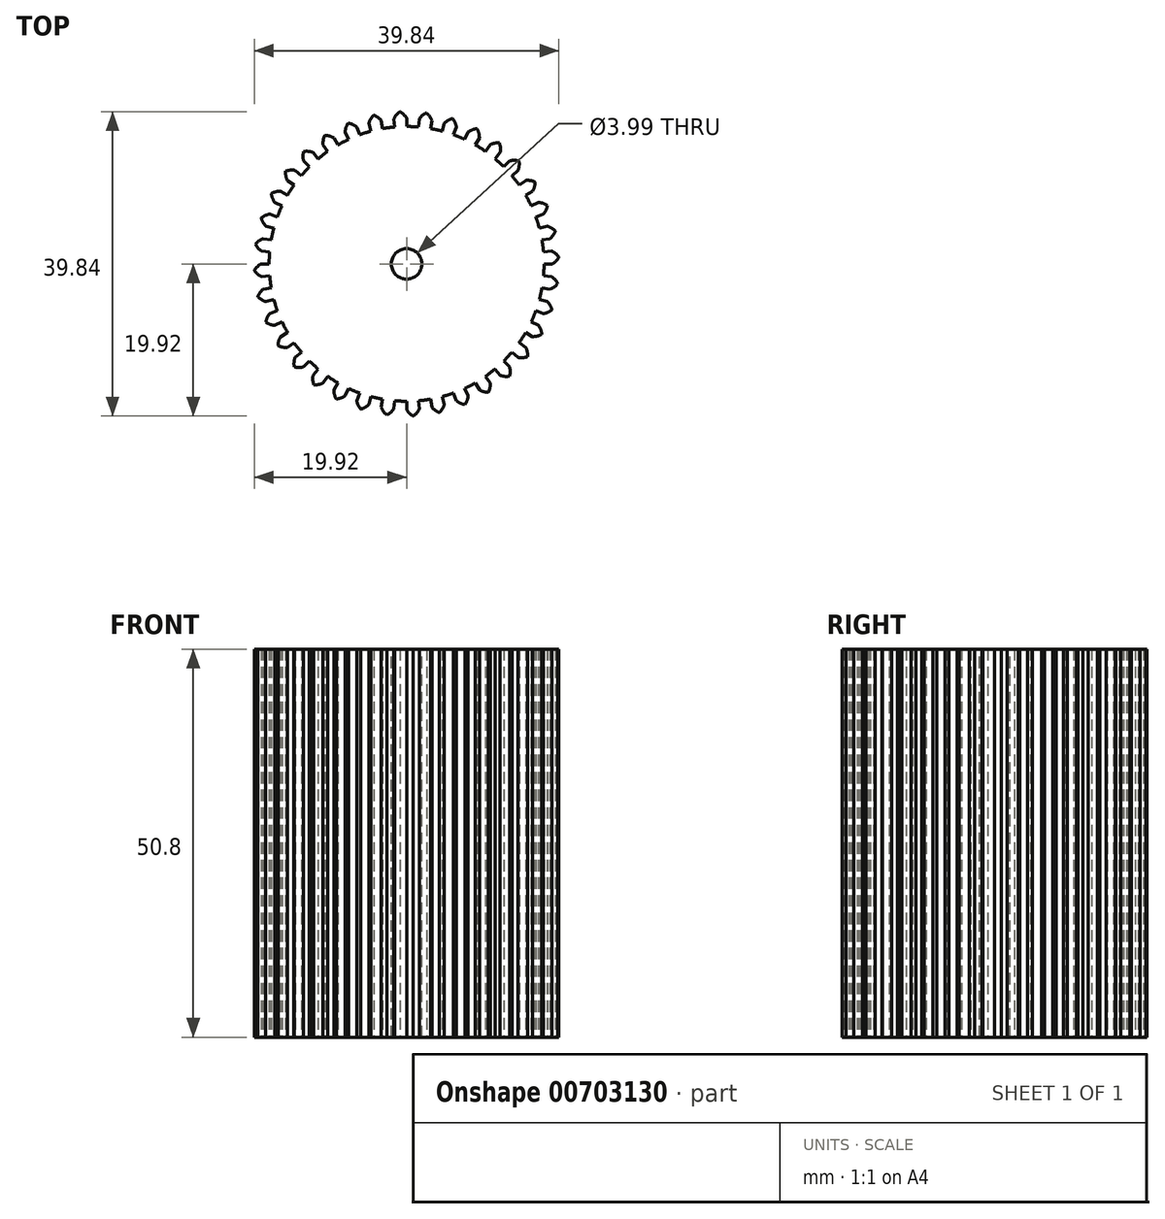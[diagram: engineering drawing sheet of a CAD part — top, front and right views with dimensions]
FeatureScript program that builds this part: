
annotation { "Feature Type Name" : "Feature", "Feature Type Description" : "" }
export const myFeature = defineFeature(function(context is Context, id is Id, definition is map)
    precondition{}
    {
        {
            var Q0;
            Q0=qCreatedBy(makeId("Top.planeOp"),FACE);
            var sketch = newSketch(context, id + "F0", { "sketchPlane" : qUnion([Q0])});
            skArc(sketch, "E0", {"start": v(-1.57, 17.91) * mm, "mid": v(0.78, -17.97) * mm, "end": v(0, 17.98) * mm});
            skPoint(sketch, "E1", {"position": v(0, 19.05) * mm});
            skArc(sketch, "E2.trimOffspring", {"start": v(0, 19.05) * mm, "mid": v(-0.38, 19.54) * mm, "end": v(-0.87, 19.92) * mm});
            skArc(sketch, "E3.trimOffspring", {"start": v(0, 16.67) * mm, "mid": v(0, 16.67) * mm, "end": v(0, 16.67) * mm});
            skArc(sketch, "E4.trimOffspring", {"start": v(-4.4, 17.45) * mm, "mid": v(-4.4, 17.44) * mm, "end": v(-4.4, 17.43) * mm});
            skArc(sketch, "E5.trimOffspring", {"start": v(0, 16.67) * mm, "mid": v(0, 16.67) * mm, "end": v(0, 16.68) * mm});
            skLineSegment(sketch, "E6", {"start": v(0, 19.05) * mm, "end": v(0, 17.98) * mm});
            skArc(sketch, "E7.MirrorCS", {"start": v(-1.66, 18.98) * mm, "mid": v(-1.33, 19.5) * mm, "end": v(-0.87, 19.92) * mm});
            skLineSegment(sketch, "E8", {"start": v(-1.66, 18.98) * mm, "end": v(-1.57, 17.91) * mm});
            skLineSegment(sketch, "E9.1.0", {"start": v(-3.3, 18.76) * mm, "end": v(-3.12, 17.7) * mm});
            skArc(sketch, "E9.1.1", {"start": v(-3.3, 18.76) * mm, "mid": v(-3.77, 19.18) * mm, "end": v(-4.32, 19.47) * mm});
            skArc(sketch, "E9.1.2", {"start": v(-4.93, 18.4) * mm, "mid": v(-4.7, 18.98) * mm, "end": v(-4.32, 19.47) * mm});
            skLineSegment(sketch, "E9.1.3", {"start": v(-4.93, 18.4) * mm, "end": v(-4.65, 17.37) * mm});
            skLineSegment(sketch, "E9.2.0", {"start": v(-6.52, 17.9) * mm, "end": v(-6.15, 16.9) * mm});
            skArc(sketch, "E9.2.1", {"start": v(-6.52, 17.9) * mm, "mid": v(-7.04, 18.24) * mm, "end": v(-7.63, 18.42) * mm});
            skArc(sketch, "E9.2.2", {"start": v(-8.05, 17.27) * mm, "mid": v(-7.92, 17.87) * mm, "end": v(-7.63, 18.42) * mm});
            skLineSegment(sketch, "E9.2.3", {"start": v(-8.05, 17.27) * mm, "end": v(-7.6, 16.3) * mm});
            skLineSegment(sketch, "E10.2.3.0", {"start": v(-9.52, 16.5) * mm, "end": v(-9, 15.57) * mm});
            skArc(sketch, "E10.3.3.0", {"start": v(-9.52, 16.5) * mm, "mid": v(-10.1, 16.74) * mm, "end": v(-10.72, 16.82) * mm});
            skArc(sketch, "E10.7.3.0", {"start": v(-10.93, 15.6) * mm, "mid": v(-10.9, 16.23) * mm, "end": v(-10.72, 16.82) * mm});
            skLineSegment(sketch, "E10.11.3.0", {"start": v(-10.93, 15.6) * mm, "end": v(-10.31, 14.73) * mm});
            skLineSegment(sketch, "E10.2.4.0", {"start": v(-12.25, 14.6) * mm, "end": v(-11.56, 13.78) * mm});
            skArc(sketch, "E10.3.4.0", {"start": v(-12.25, 14.6) * mm, "mid": v(-12.85, 14.73) * mm, "end": v(-13.47, 14.7) * mm});
            skArc(sketch, "E10.7.4.0", {"start": v(-13.47, 13.47) * mm, "mid": v(-13.55, 14.09) * mm, "end": v(-13.47, 14.7) * mm});
            skLineSegment(sketch, "E10.11.4.0", {"start": v(-13.47, 13.47) * mm, "end": v(-12.72, 12.72) * mm});
            skLineSegment(sketch, "E10.2.5.0", {"start": v(-14.6, 12.25) * mm, "end": v(-13.78, 11.56) * mm});
            skArc(sketch, "E10.3.5.0", {"start": v(-14.6, 12.25) * mm, "mid": v(-15.21, 12.27) * mm, "end": v(-15.82, 12.14) * mm});
            skArc(sketch, "E10.7.5.0", {"start": v(-15.6, 10.93) * mm, "mid": v(-15.8, 11.52) * mm, "end": v(-15.82, 12.14) * mm});
            skLineSegment(sketch, "E10.11.5.0", {"start": v(-15.6, 10.93) * mm, "end": v(-14.73, 10.31) * mm});
            skLineSegment(sketch, "E10.2.6.0", {"start": v(-16.5, 9.53) * mm, "end": v(-15.57, 9) * mm});
            skArc(sketch, "E10.3.6.0", {"start": v(-16.5, 9.53) * mm, "mid": v(-17.11, 9.45) * mm, "end": v(-17.69, 9.2) * mm});
            skArc(sketch, "E10.7.6.0", {"start": v(-17.27, 8.05) * mm, "mid": v(-17.55, 8.6) * mm, "end": v(-17.69, 9.2) * mm});
            skLineSegment(sketch, "E10.11.6.0", {"start": v(-17.27, 8.05) * mm, "end": v(-16.3, 7.6) * mm});
            skLineSegment(sketch, "E10.2.7.0", {"start": v(-17.9, 6.52) * mm, "end": v(-16.9, 6.15) * mm});
            skArc(sketch, "E10.3.7.0", {"start": v(-17.9, 6.52) * mm, "mid": v(-18.5, 6.33) * mm, "end": v(-19.02, 6) * mm});
            skArc(sketch, "E10.7.7.0", {"start": v(-18.4, 4.93) * mm, "mid": v(-18.78, 5.42) * mm, "end": v(-19.02, 6) * mm});
            skLineSegment(sketch, "E10.11.7.0", {"start": v(-18.4, 4.93) * mm, "end": v(-17.37, 4.65) * mm});
            skLineSegment(sketch, "E10.2.8.0", {"start": v(-18.76, 3.3) * mm, "end": v(-17.7, 3.12) * mm});
            skArc(sketch, "E10.3.8.0", {"start": v(-18.76, 3.3) * mm, "mid": v(-19.31, 3.02) * mm, "end": v(-19.77, 2.6) * mm});
            skArc(sketch, "E10.7.8.0", {"start": v(-18.98, 1.66) * mm, "mid": v(-19.44, 2.08) * mm, "end": v(-19.77, 2.6) * mm});
            skLineSegment(sketch, "E10.11.8.0", {"start": v(-18.98, 1.66) * mm, "end": v(-17.91, 1.57) * mm});
            skLineSegment(sketch, "E10.2.9.0", {"start": v(-19.05, 0) * mm, "end": v(-17.98, 0) * mm});
            skArc(sketch, "E10.3.9.0", {"start": v(-19.05, 0) * mm, "mid": v(-19.54, -0.38) * mm, "end": v(-19.92, -0.87) * mm});
            skArc(sketch, "E10.7.9.0", {"start": v(-18.98, -1.66) * mm, "mid": v(-19.5, -1.33) * mm, "end": v(-19.92, -0.87) * mm});
            skLineSegment(sketch, "E10.11.9.0", {"start": v(-18.98, -1.66) * mm, "end": v(-17.91, -1.57) * mm});
            skLineSegment(sketch, "E10.2.10.0", {"start": v(-18.76, -3.3) * mm, "end": v(-17.7, -3.12) * mm});
            skArc(sketch, "E10.3.10.0", {"start": v(-18.76, -3.3) * mm, "mid": v(-19.18, -3.77) * mm, "end": v(-19.47, -4.32) * mm});
            skArc(sketch, "E10.7.10.0", {"start": v(-18.4, -4.93) * mm, "mid": v(-18.98, -4.7) * mm, "end": v(-19.47, -4.32) * mm});
            skLineSegment(sketch, "E10.11.10.0", {"start": v(-18.4, -4.93) * mm, "end": v(-17.37, -4.65) * mm});
            skLineSegment(sketch, "E10.2.11.0", {"start": v(-17.9, -6.52) * mm, "end": v(-16.9, -6.15) * mm});
            skArc(sketch, "E10.3.11.0", {"start": v(-17.9, -6.52) * mm, "mid": v(-18.24, -7.04) * mm, "end": v(-18.42, -7.63) * mm});
            skArc(sketch, "E10.7.11.0", {"start": v(-17.27, -8.05) * mm, "mid": v(-17.87, -7.92) * mm, "end": v(-18.42, -7.63) * mm});
            skLineSegment(sketch, "E10.11.11.0", {"start": v(-17.27, -8.05) * mm, "end": v(-16.3, -7.6) * mm});
            skLineSegment(sketch, "E10.2.12.0", {"start": v(-16.5, -9.52) * mm, "end": v(-15.57, -9) * mm});
            skArc(sketch, "E10.3.12.0", {"start": v(-16.5, -9.52) * mm, "mid": v(-16.74, -10.1) * mm, "end": v(-16.82, -10.72) * mm});
            skArc(sketch, "E10.7.12.0", {"start": v(-15.6, -10.93) * mm, "mid": v(-16.23, -10.9) * mm, "end": v(-16.82, -10.72) * mm});
            skLineSegment(sketch, "E10.11.12.0", {"start": v(-15.6, -10.93) * mm, "end": v(-14.73, -10.31) * mm});
            skLineSegment(sketch, "E10.2.13.0", {"start": v(-14.6, -12.25) * mm, "end": v(-13.78, -11.56) * mm});
            skArc(sketch, "E10.3.13.0", {"start": v(-14.6, -12.25) * mm, "mid": v(-14.73, -12.85) * mm, "end": v(-14.7, -13.47) * mm});
            skArc(sketch, "E10.7.13.0", {"start": v(-13.47, -13.47) * mm, "mid": v(-14.09, -13.55) * mm, "end": v(-14.7, -13.47) * mm});
            skLineSegment(sketch, "E10.11.13.0", {"start": v(-13.47, -13.47) * mm, "end": v(-12.72, -12.72) * mm});
            skLineSegment(sketch, "E10.2.14.0", {"start": v(-12.25, -14.6) * mm, "end": v(-11.56, -13.78) * mm});
            skArc(sketch, "E10.3.14.0", {"start": v(-12.25, -14.6) * mm, "mid": v(-12.27, -15.21) * mm, "end": v(-12.14, -15.82) * mm});
            skArc(sketch, "E10.7.14.0", {"start": v(-10.93, -15.6) * mm, "mid": v(-11.52, -15.8) * mm, "end": v(-12.14, -15.82) * mm});
            skLineSegment(sketch, "E10.11.14.0", {"start": v(-10.93, -15.6) * mm, "end": v(-10.31, -14.73) * mm});
            skLineSegment(sketch, "E10.2.15.0", {"start": v(-9.53, -16.5) * mm, "end": v(-9, -15.57) * mm});
            skArc(sketch, "E10.3.15.0", {"start": v(-9.53, -16.5) * mm, "mid": v(-9.45, -17.11) * mm, "end": v(-9.2, -17.69) * mm});
            skArc(sketch, "E10.7.15.0", {"start": v(-8.05, -17.27) * mm, "mid": v(-8.6, -17.55) * mm, "end": v(-9.2, -17.69) * mm});
            skLineSegment(sketch, "E10.11.15.0", {"start": v(-8.05, -17.27) * mm, "end": v(-7.6, -16.3) * mm});
            skLineSegment(sketch, "E10.2.16.0", {"start": v(-6.52, -17.9) * mm, "end": v(-6.15, -16.9) * mm});
            skArc(sketch, "E10.3.16.0", {"start": v(-6.52, -17.9) * mm, "mid": v(-6.33, -18.5) * mm, "end": v(-6, -19.02) * mm});
            skArc(sketch, "E10.7.16.0", {"start": v(-4.93, -18.4) * mm, "mid": v(-5.42, -18.78) * mm, "end": v(-6, -19.02) * mm});
            skLineSegment(sketch, "E10.11.16.0", {"start": v(-4.93, -18.4) * mm, "end": v(-4.65, -17.37) * mm});
            skLineSegment(sketch, "E10.2.17.0", {"start": v(-3.3, -18.76) * mm, "end": v(-3.12, -17.7) * mm});
            skArc(sketch, "E10.3.17.0", {"start": v(-3.3, -18.76) * mm, "mid": v(-3.02, -19.31) * mm, "end": v(-2.6, -19.77) * mm});
            skArc(sketch, "E10.7.17.0", {"start": v(-1.66, -18.98) * mm, "mid": v(-2.08, -19.44) * mm, "end": v(-2.6, -19.77) * mm});
            skLineSegment(sketch, "E10.11.17.0", {"start": v(-1.66, -18.98) * mm, "end": v(-1.57, -17.91) * mm});
            skLineSegment(sketch, "E10.2.18.0", {"start": v(0, -19.05) * mm, "end": v(0, -17.98) * mm});
            skArc(sketch, "E10.3.18.0", {"start": v(0, -19.05) * mm, "mid": v(0.38, -19.54) * mm, "end": v(0.87, -19.92) * mm});
            skArc(sketch, "E10.7.18.0", {"start": v(1.66, -18.98) * mm, "mid": v(1.33, -19.5) * mm, "end": v(0.87, -19.92) * mm});
            skLineSegment(sketch, "E10.11.18.0", {"start": v(1.66, -18.98) * mm, "end": v(1.57, -17.91) * mm});
            skLineSegment(sketch, "E10.2.19.0", {"start": v(3.3, -18.76) * mm, "end": v(3.12, -17.7) * mm});
            skArc(sketch, "E10.3.19.0", {"start": v(3.3, -18.76) * mm, "mid": v(3.77, -19.18) * mm, "end": v(4.32, -19.47) * mm});
            skArc(sketch, "E10.7.19.0", {"start": v(4.93, -18.4) * mm, "mid": v(4.7, -18.98) * mm, "end": v(4.32, -19.47) * mm});
            skLineSegment(sketch, "E10.11.19.0", {"start": v(4.93, -18.4) * mm, "end": v(4.65, -17.37) * mm});
            skLineSegment(sketch, "E10.2.20.0", {"start": v(6.52, -17.9) * mm, "end": v(6.15, -16.9) * mm});
            skArc(sketch, "E10.3.20.0", {"start": v(6.52, -17.9) * mm, "mid": v(7.04, -18.24) * mm, "end": v(7.63, -18.42) * mm});
            skArc(sketch, "E10.7.20.0", {"start": v(8.05, -17.27) * mm, "mid": v(7.92, -17.87) * mm, "end": v(7.63, -18.42) * mm});
            skLineSegment(sketch, "E10.11.20.0", {"start": v(8.05, -17.27) * mm, "end": v(7.6, -16.3) * mm});
            skLineSegment(sketch, "E10.2.21.0", {"start": v(9.53, -16.5) * mm, "end": v(9, -15.57) * mm});
            skArc(sketch, "E10.3.21.0", {"start": v(9.52, -16.5) * mm, "mid": v(10.1, -16.74) * mm, "end": v(10.72, -16.82) * mm});
            skArc(sketch, "E10.7.21.0", {"start": v(10.93, -15.6) * mm, "mid": v(10.9, -16.23) * mm, "end": v(10.72, -16.82) * mm});
            skLineSegment(sketch, "E10.11.21.0", {"start": v(10.93, -15.6) * mm, "end": v(10.31, -14.73) * mm});
            skLineSegment(sketch, "E10.2.22.0", {"start": v(12.25, -14.6) * mm, "end": v(11.56, -13.78) * mm});
            skArc(sketch, "E10.3.22.0", {"start": v(12.25, -14.6) * mm, "mid": v(12.85, -14.73) * mm, "end": v(13.47, -14.7) * mm});
            skArc(sketch, "E10.7.22.0", {"start": v(13.47, -13.47) * mm, "mid": v(13.55, -14.09) * mm, "end": v(13.47, -14.7) * mm});
            skLineSegment(sketch, "E10.11.22.0", {"start": v(13.47, -13.47) * mm, "end": v(12.72, -12.72) * mm});
            skLineSegment(sketch, "E10.2.23.0", {"start": v(14.6, -12.25) * mm, "end": v(13.78, -11.56) * mm});
            skArc(sketch, "E10.3.23.0", {"start": v(14.6, -12.25) * mm, "mid": v(15.21, -12.27) * mm, "end": v(15.82, -12.14) * mm});
            skArc(sketch, "E10.7.23.0", {"start": v(15.6, -10.93) * mm, "mid": v(15.8, -11.52) * mm, "end": v(15.82, -12.14) * mm});
            skLineSegment(sketch, "E10.11.23.0", {"start": v(15.6, -10.93) * mm, "end": v(14.73, -10.31) * mm});
            skLineSegment(sketch, "E10.2.24.0", {"start": v(16.5, -9.53) * mm, "end": v(15.57, -9) * mm});
            skArc(sketch, "E10.3.24.0", {"start": v(16.5, -9.53) * mm, "mid": v(17.11, -9.45) * mm, "end": v(17.69, -9.2) * mm});
            skArc(sketch, "E10.7.24.0", {"start": v(17.27, -8.05) * mm, "mid": v(17.55, -8.6) * mm, "end": v(17.69, -9.2) * mm});
            skLineSegment(sketch, "E10.11.24.0", {"start": v(17.27, -8.05) * mm, "end": v(16.3, -7.6) * mm});
            skLineSegment(sketch, "E10.2.25.0", {"start": v(17.9, -6.52) * mm, "end": v(16.9, -6.15) * mm});
            skArc(sketch, "E10.3.25.0", {"start": v(17.9, -6.52) * mm, "mid": v(18.5, -6.33) * mm, "end": v(19.02, -6) * mm});
            skArc(sketch, "E10.7.25.0", {"start": v(18.4, -4.93) * mm, "mid": v(18.78, -5.42) * mm, "end": v(19.02, -6) * mm});
            skLineSegment(sketch, "E10.11.25.0", {"start": v(18.4, -4.93) * mm, "end": v(17.37, -4.65) * mm});
            skLineSegment(sketch, "E10.2.26.0", {"start": v(18.76, -3.3) * mm, "end": v(17.7, -3.12) * mm});
            skArc(sketch, "E10.3.26.0", {"start": v(18.76, -3.3) * mm, "mid": v(19.31, -3.02) * mm, "end": v(19.77, -2.6) * mm});
            skArc(sketch, "E10.7.26.0", {"start": v(18.98, -1.66) * mm, "mid": v(19.44, -2.08) * mm, "end": v(19.77, -2.6) * mm});
            skLineSegment(sketch, "E10.11.26.0", {"start": v(18.98, -1.66) * mm, "end": v(17.91, -1.57) * mm});
            skLineSegment(sketch, "E10.2.27.0", {"start": v(19.05, 0) * mm, "end": v(17.98, 0) * mm});
            skArc(sketch, "E10.3.27.0", {"start": v(19.05, 0) * mm, "mid": v(19.54, 0.38) * mm, "end": v(19.92, 0.87) * mm});
            skArc(sketch, "E10.7.27.0", {"start": v(18.98, 1.66) * mm, "mid": v(19.5, 1.33) * mm, "end": v(19.92, 0.87) * mm});
            skLineSegment(sketch, "E10.11.27.0", {"start": v(18.98, 1.66) * mm, "end": v(17.91, 1.57) * mm});
            skLineSegment(sketch, "E10.2.28.0", {"start": v(18.76, 3.3) * mm, "end": v(17.7, 3.12) * mm});
            skArc(sketch, "E10.3.28.0", {"start": v(18.76, 3.3) * mm, "mid": v(19.18, 3.77) * mm, "end": v(19.47, 4.32) * mm});
            skArc(sketch, "E10.7.28.0", {"start": v(18.4, 4.93) * mm, "mid": v(18.98, 4.7) * mm, "end": v(19.47, 4.32) * mm});
            skLineSegment(sketch, "E10.11.28.0", {"start": v(18.4, 4.93) * mm, "end": v(17.37, 4.65) * mm});
            skLineSegment(sketch, "E10.2.29.0", {"start": v(17.9, 6.52) * mm, "end": v(16.9, 6.15) * mm});
            skArc(sketch, "E10.3.29.0", {"start": v(17.9, 6.52) * mm, "mid": v(18.24, 7.04) * mm, "end": v(18.42, 7.63) * mm});
            skArc(sketch, "E10.7.29.0", {"start": v(17.27, 8.05) * mm, "mid": v(17.87, 7.92) * mm, "end": v(18.42, 7.63) * mm});
            skLineSegment(sketch, "E10.11.29.0", {"start": v(17.27, 8.05) * mm, "end": v(16.3, 7.6) * mm});
            skLineSegment(sketch, "E10.2.30.0", {"start": v(16.5, 9.52) * mm, "end": v(15.57, 9) * mm});
            skArc(sketch, "E10.3.30.0", {"start": v(16.5, 9.52) * mm, "mid": v(16.74, 10.1) * mm, "end": v(16.82, 10.72) * mm});
            skArc(sketch, "E10.7.30.0", {"start": v(15.6, 10.93) * mm, "mid": v(16.23, 10.9) * mm, "end": v(16.82, 10.72) * mm});
            skLineSegment(sketch, "E10.11.30.0", {"start": v(15.6, 10.93) * mm, "end": v(14.73, 10.31) * mm});
            skLineSegment(sketch, "E10.2.31.0", {"start": v(14.6, 12.25) * mm, "end": v(13.78, 11.56) * mm});
            skArc(sketch, "E10.3.31.0", {"start": v(14.6, 12.25) * mm, "mid": v(14.73, 12.85) * mm, "end": v(14.7, 13.47) * mm});
            skArc(sketch, "E10.7.31.0", {"start": v(13.47, 13.47) * mm, "mid": v(14.09, 13.55) * mm, "end": v(14.7, 13.47) * mm});
            skLineSegment(sketch, "E10.11.31.0", {"start": v(13.47, 13.47) * mm, "end": v(12.72, 12.72) * mm});
            skLineSegment(sketch, "E10.2.32.0", {"start": v(12.25, 14.6) * mm, "end": v(11.56, 13.78) * mm});
            skArc(sketch, "E10.3.32.0", {"start": v(12.25, 14.6) * mm, "mid": v(12.27, 15.21) * mm, "end": v(12.14, 15.82) * mm});
            skArc(sketch, "E10.7.32.0", {"start": v(10.93, 15.6) * mm, "mid": v(11.52, 15.8) * mm, "end": v(12.14, 15.82) * mm});
            skLineSegment(sketch, "E10.11.32.0", {"start": v(10.93, 15.6) * mm, "end": v(10.31, 14.73) * mm});
            skLineSegment(sketch, "E10.2.33.0", {"start": v(9.52, 16.5) * mm, "end": v(9, 15.57) * mm});
            skArc(sketch, "E10.3.33.0", {"start": v(9.53, 16.5) * mm, "mid": v(9.45, 17.11) * mm, "end": v(9.2, 17.69) * mm});
            skArc(sketch, "E10.7.33.0", {"start": v(8.05, 17.27) * mm, "mid": v(8.6, 17.55) * mm, "end": v(9.2, 17.69) * mm});
            skLineSegment(sketch, "E10.11.33.0", {"start": v(8.05, 17.27) * mm, "end": v(7.6, 16.3) * mm});
            skLineSegment(sketch, "E10.2.34.0", {"start": v(6.52, 17.9) * mm, "end": v(6.15, 16.9) * mm});
            skArc(sketch, "E10.3.34.0", {"start": v(6.52, 17.9) * mm, "mid": v(6.33, 18.5) * mm, "end": v(6, 19.02) * mm});
            skArc(sketch, "E10.7.34.0", {"start": v(4.93, 18.4) * mm, "mid": v(5.42, 18.78) * mm, "end": v(6, 19.02) * mm});
            skLineSegment(sketch, "E10.11.34.0", {"start": v(4.93, 18.4) * mm, "end": v(4.65, 17.37) * mm});
            skLineSegment(sketch, "E10.2.35.0", {"start": v(3.3, 18.76) * mm, "end": v(3.12, 17.7) * mm});
            skArc(sketch, "E10.3.35.0", {"start": v(3.3, 18.76) * mm, "mid": v(3.02, 19.31) * mm, "end": v(2.6, 19.77) * mm});
            skArc(sketch, "E10.7.35.0", {"start": v(1.66, 18.98) * mm, "mid": v(2.08, 19.44) * mm, "end": v(2.6, 19.77) * mm});
            skLineSegment(sketch, "E10.11.35.0", {"start": v(1.66, 18.98) * mm, "end": v(1.57, 17.91) * mm});
            skSolve(sketch);
        }
        {
            var Q0;
            Q0=makeQuery(id+"F0.imprint","IMPRINT",FACE,{"disambiguationData":[TD([[makeQuery(id+"F0.imprint","IMPRINT",EDGE,{"derivedFrom":sQuery(id+"F0.wireOp",EDGE,"E2.trimOffspring")}),1.0]])]});
            var Q1;
            {var subQ3=sQuery(id+"F0.wireOp",EDGE,"E9.1.0");Q1=makeQuery(id+"F0.imprint","IMPRINT",FACE,{"disambiguationData":[TD([[makeQuery(id+"F0.imprint","IMPRINT",EDGE,{"derivedFrom":subQ3}),-1.0]])]});}
            var Q2;
            {var subQ0=sQuery(id+"F0.wireOp",EDGE,"E10.2.28.0");Q2=makeQuery(id+"F0.imprint","IMPRINT",FACE,{"disambiguationData":[TD([[makeQuery(id+"F0.imprint","IMPRINT",EDGE,{"derivedFrom":subQ0}),-1.0]])]});}
            var Q3;
            {var subQ0=sQuery(id+"F0.wireOp",EDGE,"E10.2.30.0");Q3=makeQuery(id+"F0.imprint","IMPRINT",FACE,{"disambiguationData":[TD([[makeQuery(id+"F0.imprint","IMPRINT",EDGE,{"derivedFrom":subQ0}),-1.0]])]});}
            var Q4;
            {var subQ0=sQuery(id+"F0.wireOp",EDGE,"E10.2.27.0");Q4=makeQuery(id+"F0.imprint","IMPRINT",FACE,{"disambiguationData":[TD([[makeQuery(id+"F0.imprint","IMPRINT",EDGE,{"derivedFrom":subQ0}),-1.0]])]});}
            var Q5;
            {var subQ0=sQuery(id+"F0.wireOp",EDGE,"E10.2.31.0");Q5=makeQuery(id+"F0.imprint","IMPRINT",FACE,{"disambiguationData":[TD([[makeQuery(id+"F0.imprint","IMPRINT",EDGE,{"derivedFrom":subQ0}),-1.0]])]});}
            var Q6;
            {var subQ0=sQuery(id+"F0.wireOp",EDGE,"E10.2.29.0");Q6=makeQuery(id+"F0.imprint","IMPRINT",FACE,{"disambiguationData":[TD([[makeQuery(id+"F0.imprint","IMPRINT",EDGE,{"derivedFrom":subQ0}),-1.0]])]});}
            var Q7;
            {var subQ0=sQuery(id+"F0.wireOp",EDGE,"E10.2.17.0");Q7=makeQuery(id+"F0.imprint","IMPRINT",FACE,{"disambiguationData":[TD([[makeQuery(id+"F0.imprint","IMPRINT",EDGE,{"derivedFrom":subQ0}),-1.0]])]});}
            var Q8;
            {var subQ0=sQuery(id+"F0.wireOp",EDGE,"E10.2.33.0");Q8=makeQuery(id+"F0.imprint","IMPRINT",FACE,{"disambiguationData":[TD([[makeQuery(id+"F0.imprint","IMPRINT",EDGE,{"derivedFrom":subQ0}),-1.0]])]});}
            var Q9;
            {var subQ0=sQuery(id+"F0.wireOp",EDGE,"E10.2.18.0");Q9=makeQuery(id+"F0.imprint","IMPRINT",FACE,{"disambiguationData":[TD([[makeQuery(id+"F0.imprint","IMPRINT",EDGE,{"derivedFrom":subQ0}),-1.0]])]});}
            var Q10;
            {var subQ0=sQuery(id+"F0.wireOp",EDGE,"E10.2.34.0");Q10=makeQuery(id+"F0.imprint","IMPRINT",FACE,{"disambiguationData":[TD([[makeQuery(id+"F0.imprint","IMPRINT",EDGE,{"derivedFrom":subQ0}),-1.0]])]});}
            var Q11;
            {var subQ0=sQuery(id+"F0.wireOp",EDGE,"E10.2.19.0");Q11=makeQuery(id+"F0.imprint","IMPRINT",FACE,{"disambiguationData":[TD([[makeQuery(id+"F0.imprint","IMPRINT",EDGE,{"derivedFrom":subQ0}),-1.0]])]});}
            var Q12;
            {var subQ0=sQuery(id+"F0.wireOp",EDGE,"E10.2.35.0");Q12=makeQuery(id+"F0.imprint","IMPRINT",FACE,{"disambiguationData":[TD([[makeQuery(id+"F0.imprint","IMPRINT",EDGE,{"derivedFrom":subQ0}),-1.0]])]});}
            var Q13;
            {var subQ0=sQuery(id+"F0.wireOp",EDGE,"E10.2.20.0");Q13=makeQuery(id+"F0.imprint","IMPRINT",FACE,{"disambiguationData":[TD([[makeQuery(id+"F0.imprint","IMPRINT",EDGE,{"derivedFrom":subQ0}),-1.0]])]});}
            var Q14;
            {var subQ0=sQuery(id+"F0.wireOp",EDGE,"E10.2.21.0");Q14=makeQuery(id+"F0.imprint","IMPRINT",FACE,{"disambiguationData":[TD([[makeQuery(id+"F0.imprint","IMPRINT",EDGE,{"derivedFrom":subQ0}),-1.0]])]});}
            var Q15;
            {var subQ0=sQuery(id+"F0.wireOp",EDGE,"E10.2.22.0");Q15=makeQuery(id+"F0.imprint","IMPRINT",FACE,{"disambiguationData":[TD([[makeQuery(id+"F0.imprint","IMPRINT",EDGE,{"derivedFrom":subQ0}),-1.0]])]});}
            var Q16;
            {var subQ0=sQuery(id+"F0.wireOp",EDGE,"E10.2.23.0");Q16=makeQuery(id+"F0.imprint","IMPRINT",FACE,{"disambiguationData":[TD([[makeQuery(id+"F0.imprint","IMPRINT",EDGE,{"derivedFrom":subQ0}),-1.0]])]});}
            var Q17;
            {var subQ0=sQuery(id+"F0.wireOp",EDGE,"E10.2.16.0");Q17=makeQuery(id+"F0.imprint","IMPRINT",FACE,{"disambiguationData":[TD([[makeQuery(id+"F0.imprint","IMPRINT",EDGE,{"derivedFrom":subQ0}),-1.0]])]});}
            var Q18;
            {var subQ0=sQuery(id+"F0.wireOp",EDGE,"E10.2.14.0");Q18=makeQuery(id+"F0.imprint","IMPRINT",FACE,{"disambiguationData":[TD([[makeQuery(id+"F0.imprint","IMPRINT",EDGE,{"derivedFrom":subQ0}),-1.0]])]});}
            var Q19;
            {var subQ0=sQuery(id+"F0.wireOp",EDGE,"E10.2.15.0");Q19=makeQuery(id+"F0.imprint","IMPRINT",FACE,{"disambiguationData":[TD([[makeQuery(id+"F0.imprint","IMPRINT",EDGE,{"derivedFrom":subQ0}),-1.0]])]});}
            var Q20;
            {var subQ0=sQuery(id+"F0.wireOp",EDGE,"E9.2.0");Q20=makeQuery(id+"F0.imprint","IMPRINT",FACE,{"disambiguationData":[TD([[makeQuery(id+"F0.imprint","IMPRINT",EDGE,{"derivedFrom":subQ0}),-1.0]])]});}
            var Q21;
            {var subQ0=sQuery(id+"F0.wireOp",EDGE,"E10.2.3.0");Q21=makeQuery(id+"F0.imprint","IMPRINT",FACE,{"disambiguationData":[TD([[makeQuery(id+"F0.imprint","IMPRINT",EDGE,{"derivedFrom":subQ0}),-1.0]])]});}
            var Q22;
            {var subQ0=sQuery(id+"F0.wireOp",EDGE,"E10.2.4.0");Q22=makeQuery(id+"F0.imprint","IMPRINT",FACE,{"disambiguationData":[TD([[makeQuery(id+"F0.imprint","IMPRINT",EDGE,{"derivedFrom":subQ0}),-1.0]])]});}
            var Q23;
            {var subQ0=sQuery(id+"F0.wireOp",EDGE,"E10.2.5.0");Q23=makeQuery(id+"F0.imprint","IMPRINT",FACE,{"disambiguationData":[TD([[makeQuery(id+"F0.imprint","IMPRINT",EDGE,{"derivedFrom":subQ0}),-1.0]])]});}
            var Q24;
            {var subQ0=sQuery(id+"F0.wireOp",EDGE,"E10.2.6.0");Q24=makeQuery(id+"F0.imprint","IMPRINT",FACE,{"disambiguationData":[TD([[makeQuery(id+"F0.imprint","IMPRINT",EDGE,{"derivedFrom":subQ0}),-1.0]])]});}
            var Q25;
            {var subQ0=sQuery(id+"F0.wireOp",EDGE,"E10.2.7.0");Q25=makeQuery(id+"F0.imprint","IMPRINT",FACE,{"disambiguationData":[TD([[makeQuery(id+"F0.imprint","IMPRINT",EDGE,{"derivedFrom":subQ0}),-1.0]])]});}
            var Q26;
            {var subQ0=sQuery(id+"F0.wireOp",EDGE,"E10.2.8.0");Q26=makeQuery(id+"F0.imprint","IMPRINT",FACE,{"disambiguationData":[TD([[makeQuery(id+"F0.imprint","IMPRINT",EDGE,{"derivedFrom":subQ0}),-1.0]])]});}
            var Q27;
            {var subQ0=sQuery(id+"F0.wireOp",EDGE,"E10.2.9.0");Q27=makeQuery(id+"F0.imprint","IMPRINT",FACE,{"disambiguationData":[TD([[makeQuery(id+"F0.imprint","IMPRINT",EDGE,{"derivedFrom":subQ0}),-1.0]])]});}
            var Q28;
            {var subQ0=sQuery(id+"F0.wireOp",EDGE,"E10.2.10.0");Q28=makeQuery(id+"F0.imprint","IMPRINT",FACE,{"disambiguationData":[TD([[makeQuery(id+"F0.imprint","IMPRINT",EDGE,{"derivedFrom":subQ0}),-1.0]])]});}
            var Q29;
            {var subQ0=sQuery(id+"F0.wireOp",EDGE,"E10.2.11.0");Q29=makeQuery(id+"F0.imprint","IMPRINT",FACE,{"disambiguationData":[TD([[makeQuery(id+"F0.imprint","IMPRINT",EDGE,{"derivedFrom":subQ0}),-1.0]])]});}
            var Q30;
            {var subQ0=sQuery(id+"F0.wireOp",EDGE,"E10.2.12.0");Q30=makeQuery(id+"F0.imprint","IMPRINT",FACE,{"disambiguationData":[TD([[makeQuery(id+"F0.imprint","IMPRINT",EDGE,{"derivedFrom":subQ0}),-1.0]])]});}
            var Q31;
            {var subQ0=sQuery(id+"F0.wireOp",EDGE,"E10.2.13.0");Q31=makeQuery(id+"F0.imprint","IMPRINT",FACE,{"disambiguationData":[TD([[makeQuery(id+"F0.imprint","IMPRINT",EDGE,{"derivedFrom":subQ0}),-1.0]])]});}
            var Q32;
            {var subQ0=sQuery(id+"F0.wireOp",EDGE,"E10.2.24.0");Q32=makeQuery(id+"F0.imprint","IMPRINT",FACE,{"disambiguationData":[TD([[makeQuery(id+"F0.imprint","IMPRINT",EDGE,{"derivedFrom":subQ0}),-1.0]])]});}
            var Q33;
            {var subQ0=sQuery(id+"F0.wireOp",EDGE,"E10.2.25.0");Q33=makeQuery(id+"F0.imprint","IMPRINT",FACE,{"disambiguationData":[TD([[makeQuery(id+"F0.imprint","IMPRINT",EDGE,{"derivedFrom":subQ0}),-1.0]])]});}
            var Q34;
            {var subQ0=sQuery(id+"F0.wireOp",EDGE,"E10.2.32.0");Q34=makeQuery(id+"F0.imprint","IMPRINT",FACE,{"disambiguationData":[TD([[makeQuery(id+"F0.imprint","IMPRINT",EDGE,{"derivedFrom":subQ0}),-1.0]])]});}
            var Q35;
            {var subQ0=sQuery(id+"F0.wireOp",EDGE,"E10.2.26.0");Q35=makeQuery(id+"F0.imprint","IMPRINT",FACE,{"disambiguationData":[TD([[makeQuery(id+"F0.imprint","IMPRINT",EDGE,{"derivedFrom":subQ0}),-1.0]])]});}
            extrude(context, id + "F1", {"entities" : qUnion([Q0, Q1, Q2, Q3, Q4, Q5, Q6, Q7, Q8, Q9, Q10, Q11, Q12, Q13, Q14, Q15, Q16, Q17, Q18, Q19, Q20, Q21, Q22, Q23, Q24, Q25, Q26, Q27, Q28, Q29, Q30, Q31, Q32, Q33, Q34, Q35]), "depth" : 50.8 * mm, "offsetDistance" : 25.4 * mm});
        }
        {
            var Q0;
            Q0=makeQuery(id+"F1.opExtrude","CAP_FACE",FACE,{"disambiguationData":[OSD([sQuery(id+"F0.wireOp",EDGE,"E0"),sQuery(id+"F0.wireOp",EDGE,"E2.trimOffspring"),sQuery(id+"F0.wireOp",EDGE,"E6"),sQuery(id+"F0.wireOp",EDGE,"E7.MirrorCS"),sQuery(id+"F0.wireOp",EDGE,"E8"),sQuery(id+"F0.wireOp",EDGE,"E9.1.0"),sQuery(id+"F0.wireOp",EDGE,"E9.1.1"),sQuery(id+"F0.wireOp",EDGE,"E9.1.2"),sQuery(id+"F0.wireOp",EDGE,"E9.1.3"),sQuery(id+"F0.wireOp",EDGE,"E9.2.0"),sQuery(id+"F0.wireOp",EDGE,"E9.2.1"),sQuery(id+"F0.wireOp",EDGE,"E9.2.2"),sQuery(id+"F0.wireOp",EDGE,"E9.2.3"),sQuery(id+"F0.wireOp",EDGE,"E10.2.3.0"),sQuery(id+"F0.wireOp",EDGE,"E10.3.3.0"),sQuery(id+"F0.wireOp",EDGE,"E10.7.3.0"),sQuery(id+"F0.wireOp",EDGE,"E10.11.3.0"),sQuery(id+"F0.wireOp",EDGE,"E10.2.4.0"),sQuery(id+"F0.wireOp",EDGE,"E10.3.4.0"),sQuery(id+"F0.wireOp",EDGE,"E10.7.4.0"),sQuery(id+"F0.wireOp",EDGE,"E10.11.4.0"),sQuery(id+"F0.wireOp",EDGE,"E10.2.5.0"),sQuery(id+"F0.wireOp",EDGE,"E10.3.5.0"),sQuery(id+"F0.wireOp",EDGE,"E10.7.5.0"),sQuery(id+"F0.wireOp",EDGE,"E10.11.5.0"),sQuery(id+"F0.wireOp",EDGE,"E10.2.6.0"),sQuery(id+"F0.wireOp",EDGE,"E10.3.6.0"),sQuery(id+"F0.wireOp",EDGE,"E10.7.6.0"),sQuery(id+"F0.wireOp",EDGE,"E10.11.6.0"),sQuery(id+"F0.wireOp",EDGE,"E10.2.7.0"),sQuery(id+"F0.wireOp",EDGE,"E10.3.7.0"),sQuery(id+"F0.wireOp",EDGE,"E10.7.7.0"),sQuery(id+"F0.wireOp",EDGE,"E10.11.7.0"),sQuery(id+"F0.wireOp",EDGE,"E10.2.8.0"),sQuery(id+"F0.wireOp",EDGE,"E10.3.8.0"),sQuery(id+"F0.wireOp",EDGE,"E10.7.8.0"),sQuery(id+"F0.wireOp",EDGE,"E10.11.8.0"),sQuery(id+"F0.wireOp",EDGE,"E10.2.9.0"),sQuery(id+"F0.wireOp",EDGE,"E10.3.9.0"),sQuery(id+"F0.wireOp",EDGE,"E10.7.9.0"),sQuery(id+"F0.wireOp",EDGE,"E10.11.9.0"),sQuery(id+"F0.wireOp",EDGE,"E10.2.10.0"),sQuery(id+"F0.wireOp",EDGE,"E10.3.10.0"),sQuery(id+"F0.wireOp",EDGE,"E10.7.10.0"),sQuery(id+"F0.wireOp",EDGE,"E10.11.10.0"),sQuery(id+"F0.wireOp",EDGE,"E10.2.11.0"),sQuery(id+"F0.wireOp",EDGE,"E10.3.11.0"),sQuery(id+"F0.wireOp",EDGE,"E10.7.11.0"),sQuery(id+"F0.wireOp",EDGE,"E10.11.11.0"),sQuery(id+"F0.wireOp",EDGE,"E10.2.12.0"),sQuery(id+"F0.wireOp",EDGE,"E10.3.12.0"),sQuery(id+"F0.wireOp",EDGE,"E10.7.12.0"),sQuery(id+"F0.wireOp",EDGE,"E10.11.12.0"),sQuery(id+"F0.wireOp",EDGE,"E10.2.13.0"),sQuery(id+"F0.wireOp",EDGE,"E10.3.13.0"),sQuery(id+"F0.wireOp",EDGE,"E10.7.13.0"),sQuery(id+"F0.wireOp",EDGE,"E10.11.13.0"),sQuery(id+"F0.wireOp",EDGE,"E10.2.14.0"),sQuery(id+"F0.wireOp",EDGE,"E10.3.14.0"),sQuery(id+"F0.wireOp",EDGE,"E10.7.14.0"),sQuery(id+"F0.wireOp",EDGE,"E10.11.14.0"),sQuery(id+"F0.wireOp",EDGE,"E10.2.15.0"),sQuery(id+"F0.wireOp",EDGE,"E10.3.15.0"),sQuery(id+"F0.wireOp",EDGE,"E10.7.15.0"),sQuery(id+"F0.wireOp",EDGE,"E10.11.15.0"),sQuery(id+"F0.wireOp",EDGE,"E10.2.16.0"),sQuery(id+"F0.wireOp",EDGE,"E10.3.16.0"),sQuery(id+"F0.wireOp",EDGE,"E10.7.16.0"),sQuery(id+"F0.wireOp",EDGE,"E10.11.16.0"),sQuery(id+"F0.wireOp",EDGE,"E10.2.17.0"),sQuery(id+"F0.wireOp",EDGE,"E10.3.17.0"),sQuery(id+"F0.wireOp",EDGE,"E10.7.17.0"),sQuery(id+"F0.wireOp",EDGE,"E10.11.17.0"),sQuery(id+"F0.wireOp",EDGE,"E10.2.18.0"),sQuery(id+"F0.wireOp",EDGE,"E10.3.18.0"),sQuery(id+"F0.wireOp",EDGE,"E10.7.18.0"),sQuery(id+"F0.wireOp",EDGE,"E10.11.18.0"),sQuery(id+"F0.wireOp",EDGE,"E10.2.19.0"),sQuery(id+"F0.wireOp",EDGE,"E10.3.19.0"),sQuery(id+"F0.wireOp",EDGE,"E10.7.19.0"),sQuery(id+"F0.wireOp",EDGE,"E10.11.19.0"),sQuery(id+"F0.wireOp",EDGE,"E10.2.20.0"),sQuery(id+"F0.wireOp",EDGE,"E10.3.20.0"),sQuery(id+"F0.wireOp",EDGE,"E10.7.20.0"),sQuery(id+"F0.wireOp",EDGE,"E10.11.20.0"),sQuery(id+"F0.wireOp",EDGE,"E10.2.21.0"),sQuery(id+"F0.wireOp",EDGE,"E10.3.21.0"),sQuery(id+"F0.wireOp",EDGE,"E10.7.21.0"),sQuery(id+"F0.wireOp",EDGE,"E10.11.21.0"),sQuery(id+"F0.wireOp",EDGE,"E10.2.22.0"),sQuery(id+"F0.wireOp",EDGE,"E10.3.22.0"),sQuery(id+"F0.wireOp",EDGE,"E10.7.22.0"),sQuery(id+"F0.wireOp",EDGE,"E10.11.22.0"),sQuery(id+"F0.wireOp",EDGE,"E10.2.23.0"),sQuery(id+"F0.wireOp",EDGE,"E10.3.23.0"),sQuery(id+"F0.wireOp",EDGE,"E10.7.23.0"),sQuery(id+"F0.wireOp",EDGE,"E10.11.23.0"),sQuery(id+"F0.wireOp",EDGE,"E10.2.24.0"),sQuery(id+"F0.wireOp",EDGE,"E10.3.24.0"),sQuery(id+"F0.wireOp",EDGE,"E10.7.24.0"),sQuery(id+"F0.wireOp",EDGE,"E10.11.24.0"),sQuery(id+"F0.wireOp",EDGE,"E10.2.25.0"),sQuery(id+"F0.wireOp",EDGE,"E10.3.25.0"),sQuery(id+"F0.wireOp",EDGE,"E10.7.25.0"),sQuery(id+"F0.wireOp",EDGE,"E10.11.25.0"),sQuery(id+"F0.wireOp",EDGE,"E10.2.26.0"),sQuery(id+"F0.wireOp",EDGE,"E10.3.26.0"),sQuery(id+"F0.wireOp",EDGE,"E10.7.26.0"),sQuery(id+"F0.wireOp",EDGE,"E10.11.26.0"),sQuery(id+"F0.wireOp",EDGE,"E10.2.27.0"),sQuery(id+"F0.wireOp",EDGE,"E10.3.27.0"),sQuery(id+"F0.wireOp",EDGE,"E10.7.27.0"),sQuery(id+"F0.wireOp",EDGE,"E10.11.27.0"),sQuery(id+"F0.wireOp",EDGE,"E10.2.28.0"),sQuery(id+"F0.wireOp",EDGE,"E10.3.28.0"),sQuery(id+"F0.wireOp",EDGE,"E10.7.28.0"),sQuery(id+"F0.wireOp",EDGE,"E10.11.28.0"),sQuery(id+"F0.wireOp",EDGE,"E10.2.29.0"),sQuery(id+"F0.wireOp",EDGE,"E10.3.29.0"),sQuery(id+"F0.wireOp",EDGE,"E10.7.29.0"),sQuery(id+"F0.wireOp",EDGE,"E10.11.29.0"),sQuery(id+"F0.wireOp",EDGE,"E10.2.30.0"),sQuery(id+"F0.wireOp",EDGE,"E10.3.30.0"),sQuery(id+"F0.wireOp",EDGE,"E10.7.30.0"),sQuery(id+"F0.wireOp",EDGE,"E10.11.30.0"),sQuery(id+"F0.wireOp",EDGE,"E10.2.31.0"),sQuery(id+"F0.wireOp",EDGE,"E10.3.31.0"),sQuery(id+"F0.wireOp",EDGE,"E10.7.31.0"),sQuery(id+"F0.wireOp",EDGE,"E10.11.31.0"),sQuery(id+"F0.wireOp",EDGE,"E10.2.32.0"),sQuery(id+"F0.wireOp",EDGE,"E10.3.32.0"),sQuery(id+"F0.wireOp",EDGE,"E10.7.32.0"),sQuery(id+"F0.wireOp",EDGE,"E10.11.32.0"),sQuery(id+"F0.wireOp",EDGE,"E10.2.33.0"),sQuery(id+"F0.wireOp",EDGE,"E10.3.33.0"),sQuery(id+"F0.wireOp",EDGE,"E10.7.33.0"),sQuery(id+"F0.wireOp",EDGE,"E10.11.33.0"),sQuery(id+"F0.wireOp",EDGE,"E10.2.34.0"),sQuery(id+"F0.wireOp",EDGE,"E10.3.34.0"),sQuery(id+"F0.wireOp",EDGE,"E10.7.34.0"),sQuery(id+"F0.wireOp",EDGE,"E10.11.34.0"),sQuery(id+"F0.wireOp",EDGE,"E10.2.35.0"),sQuery(id+"F0.wireOp",EDGE,"E10.3.35.0"),sQuery(id+"F0.wireOp",EDGE,"E10.7.35.0"),sQuery(id+"F0.wireOp",EDGE,"E10.11.35.0")])],"isStart":false});
            var sketch = newSketch(context, id + "F2", { "sketchPlane" : qUnion([Q0])});
            skPoint(sketch, "E11", {"position": v(0, 0) * mm});
            skSolve(sketch);
        }
        {
            var Q0;
            Q0=sQuery(id+"F2.wireOp",VERTEX,"E11");
            var Q1;
            Q1=makeQuery(id+"F1.opExtrude","SWEPT_BODY",BODY,{"disambiguationData":[OSD([sQuery(id+"F0.wireOp",EDGE,"E0"),sQuery(id+"F0.wireOp",EDGE,"E2.trimOffspring"),sQuery(id+"F0.wireOp",EDGE,"E6"),sQuery(id+"F0.wireOp",EDGE,"E7.MirrorCS"),sQuery(id+"F0.wireOp",EDGE,"E8"),sQuery(id+"F0.wireOp",EDGE,"E9.1.0"),sQuery(id+"F0.wireOp",EDGE,"E9.1.1"),sQuery(id+"F0.wireOp",EDGE,"E9.1.2"),sQuery(id+"F0.wireOp",EDGE,"E9.1.3"),sQuery(id+"F0.wireOp",EDGE,"E9.2.0"),sQuery(id+"F0.wireOp",EDGE,"E9.2.1"),sQuery(id+"F0.wireOp",EDGE,"E9.2.2"),sQuery(id+"F0.wireOp",EDGE,"E9.2.3"),sQuery(id+"F0.wireOp",EDGE,"E10.2.3.0"),sQuery(id+"F0.wireOp",EDGE,"E10.3.3.0"),sQuery(id+"F0.wireOp",EDGE,"E10.7.3.0"),sQuery(id+"F0.wireOp",EDGE,"E10.11.3.0"),sQuery(id+"F0.wireOp",EDGE,"E10.2.4.0"),sQuery(id+"F0.wireOp",EDGE,"E10.3.4.0"),sQuery(id+"F0.wireOp",EDGE,"E10.7.4.0"),sQuery(id+"F0.wireOp",EDGE,"E10.11.4.0"),sQuery(id+"F0.wireOp",EDGE,"E10.2.5.0"),sQuery(id+"F0.wireOp",EDGE,"E10.3.5.0"),sQuery(id+"F0.wireOp",EDGE,"E10.7.5.0"),sQuery(id+"F0.wireOp",EDGE,"E10.11.5.0"),sQuery(id+"F0.wireOp",EDGE,"E10.2.6.0"),sQuery(id+"F0.wireOp",EDGE,"E10.3.6.0"),sQuery(id+"F0.wireOp",EDGE,"E10.7.6.0"),sQuery(id+"F0.wireOp",EDGE,"E10.11.6.0"),sQuery(id+"F0.wireOp",EDGE,"E10.2.7.0"),sQuery(id+"F0.wireOp",EDGE,"E10.3.7.0"),sQuery(id+"F0.wireOp",EDGE,"E10.7.7.0"),sQuery(id+"F0.wireOp",EDGE,"E10.11.7.0"),sQuery(id+"F0.wireOp",EDGE,"E10.2.8.0"),sQuery(id+"F0.wireOp",EDGE,"E10.3.8.0"),sQuery(id+"F0.wireOp",EDGE,"E10.7.8.0"),sQuery(id+"F0.wireOp",EDGE,"E10.11.8.0"),sQuery(id+"F0.wireOp",EDGE,"E10.2.9.0"),sQuery(id+"F0.wireOp",EDGE,"E10.3.9.0"),sQuery(id+"F0.wireOp",EDGE,"E10.7.9.0"),sQuery(id+"F0.wireOp",EDGE,"E10.11.9.0"),sQuery(id+"F0.wireOp",EDGE,"E10.2.10.0"),sQuery(id+"F0.wireOp",EDGE,"E10.3.10.0"),sQuery(id+"F0.wireOp",EDGE,"E10.7.10.0"),sQuery(id+"F0.wireOp",EDGE,"E10.11.10.0"),sQuery(id+"F0.wireOp",EDGE,"E10.2.11.0"),sQuery(id+"F0.wireOp",EDGE,"E10.3.11.0"),sQuery(id+"F0.wireOp",EDGE,"E10.7.11.0"),sQuery(id+"F0.wireOp",EDGE,"E10.11.11.0"),sQuery(id+"F0.wireOp",EDGE,"E10.2.12.0"),sQuery(id+"F0.wireOp",EDGE,"E10.3.12.0"),sQuery(id+"F0.wireOp",EDGE,"E10.7.12.0"),sQuery(id+"F0.wireOp",EDGE,"E10.11.12.0"),sQuery(id+"F0.wireOp",EDGE,"E10.2.13.0"),sQuery(id+"F0.wireOp",EDGE,"E10.3.13.0"),sQuery(id+"F0.wireOp",EDGE,"E10.7.13.0"),sQuery(id+"F0.wireOp",EDGE,"E10.11.13.0"),sQuery(id+"F0.wireOp",EDGE,"E10.2.14.0"),sQuery(id+"F0.wireOp",EDGE,"E10.3.14.0"),sQuery(id+"F0.wireOp",EDGE,"E10.7.14.0"),sQuery(id+"F0.wireOp",EDGE,"E10.11.14.0"),sQuery(id+"F0.wireOp",EDGE,"E10.2.15.0"),sQuery(id+"F0.wireOp",EDGE,"E10.3.15.0"),sQuery(id+"F0.wireOp",EDGE,"E10.7.15.0"),sQuery(id+"F0.wireOp",EDGE,"E10.11.15.0"),sQuery(id+"F0.wireOp",EDGE,"E10.2.16.0"),sQuery(id+"F0.wireOp",EDGE,"E10.3.16.0"),sQuery(id+"F0.wireOp",EDGE,"E10.7.16.0"),sQuery(id+"F0.wireOp",EDGE,"E10.11.16.0"),sQuery(id+"F0.wireOp",EDGE,"E10.2.17.0"),sQuery(id+"F0.wireOp",EDGE,"E10.3.17.0"),sQuery(id+"F0.wireOp",EDGE,"E10.7.17.0"),sQuery(id+"F0.wireOp",EDGE,"E10.11.17.0"),sQuery(id+"F0.wireOp",EDGE,"E10.2.18.0"),sQuery(id+"F0.wireOp",EDGE,"E10.3.18.0"),sQuery(id+"F0.wireOp",EDGE,"E10.7.18.0"),sQuery(id+"F0.wireOp",EDGE,"E10.11.18.0"),sQuery(id+"F0.wireOp",EDGE,"E10.2.19.0"),sQuery(id+"F0.wireOp",EDGE,"E10.3.19.0"),sQuery(id+"F0.wireOp",EDGE,"E10.7.19.0"),sQuery(id+"F0.wireOp",EDGE,"E10.11.19.0"),sQuery(id+"F0.wireOp",EDGE,"E10.2.20.0"),sQuery(id+"F0.wireOp",EDGE,"E10.3.20.0"),sQuery(id+"F0.wireOp",EDGE,"E10.7.20.0"),sQuery(id+"F0.wireOp",EDGE,"E10.11.20.0"),sQuery(id+"F0.wireOp",EDGE,"E10.2.21.0"),sQuery(id+"F0.wireOp",EDGE,"E10.3.21.0"),sQuery(id+"F0.wireOp",EDGE,"E10.7.21.0"),sQuery(id+"F0.wireOp",EDGE,"E10.11.21.0"),sQuery(id+"F0.wireOp",EDGE,"E10.2.22.0"),sQuery(id+"F0.wireOp",EDGE,"E10.3.22.0"),sQuery(id+"F0.wireOp",EDGE,"E10.7.22.0"),sQuery(id+"F0.wireOp",EDGE,"E10.11.22.0"),sQuery(id+"F0.wireOp",EDGE,"E10.2.23.0"),sQuery(id+"F0.wireOp",EDGE,"E10.3.23.0"),sQuery(id+"F0.wireOp",EDGE,"E10.7.23.0"),sQuery(id+"F0.wireOp",EDGE,"E10.11.23.0"),sQuery(id+"F0.wireOp",EDGE,"E10.2.24.0"),sQuery(id+"F0.wireOp",EDGE,"E10.3.24.0"),sQuery(id+"F0.wireOp",EDGE,"E10.7.24.0"),sQuery(id+"F0.wireOp",EDGE,"E10.11.24.0"),sQuery(id+"F0.wireOp",EDGE,"E10.2.25.0"),sQuery(id+"F0.wireOp",EDGE,"E10.3.25.0"),sQuery(id+"F0.wireOp",EDGE,"E10.7.25.0"),sQuery(id+"F0.wireOp",EDGE,"E10.11.25.0"),sQuery(id+"F0.wireOp",EDGE,"E10.2.26.0"),sQuery(id+"F0.wireOp",EDGE,"E10.3.26.0"),sQuery(id+"F0.wireOp",EDGE,"E10.7.26.0"),sQuery(id+"F0.wireOp",EDGE,"E10.11.26.0"),sQuery(id+"F0.wireOp",EDGE,"E10.2.27.0"),sQuery(id+"F0.wireOp",EDGE,"E10.3.27.0"),sQuery(id+"F0.wireOp",EDGE,"E10.7.27.0"),sQuery(id+"F0.wireOp",EDGE,"E10.11.27.0"),sQuery(id+"F0.wireOp",EDGE,"E10.2.28.0"),sQuery(id+"F0.wireOp",EDGE,"E10.3.28.0"),sQuery(id+"F0.wireOp",EDGE,"E10.7.28.0"),sQuery(id+"F0.wireOp",EDGE,"E10.11.28.0"),sQuery(id+"F0.wireOp",EDGE,"E10.2.29.0"),sQuery(id+"F0.wireOp",EDGE,"E10.3.29.0"),sQuery(id+"F0.wireOp",EDGE,"E10.7.29.0"),sQuery(id+"F0.wireOp",EDGE,"E10.11.29.0"),sQuery(id+"F0.wireOp",EDGE,"E10.2.30.0"),sQuery(id+"F0.wireOp",EDGE,"E10.3.30.0"),sQuery(id+"F0.wireOp",EDGE,"E10.7.30.0"),sQuery(id+"F0.wireOp",EDGE,"E10.11.30.0"),sQuery(id+"F0.wireOp",EDGE,"E10.2.31.0"),sQuery(id+"F0.wireOp",EDGE,"E10.3.31.0"),sQuery(id+"F0.wireOp",EDGE,"E10.7.31.0"),sQuery(id+"F0.wireOp",EDGE,"E10.11.31.0"),sQuery(id+"F0.wireOp",EDGE,"E10.2.32.0"),sQuery(id+"F0.wireOp",EDGE,"E10.3.32.0"),sQuery(id+"F0.wireOp",EDGE,"E10.7.32.0"),sQuery(id+"F0.wireOp",EDGE,"E10.11.32.0"),sQuery(id+"F0.wireOp",EDGE,"E10.2.33.0"),sQuery(id+"F0.wireOp",EDGE,"E10.3.33.0"),sQuery(id+"F0.wireOp",EDGE,"E10.7.33.0"),sQuery(id+"F0.wireOp",EDGE,"E10.11.33.0"),sQuery(id+"F0.wireOp",EDGE,"E10.2.34.0"),sQuery(id+"F0.wireOp",EDGE,"E10.3.34.0"),sQuery(id+"F0.wireOp",EDGE,"E10.7.34.0"),sQuery(id+"F0.wireOp",EDGE,"E10.11.34.0"),sQuery(id+"F0.wireOp",EDGE,"E10.2.35.0"),sQuery(id+"F0.wireOp",EDGE,"E10.3.35.0"),sQuery(id+"F0.wireOp",EDGE,"E10.7.35.0"),sQuery(id+"F0.wireOp",EDGE,"E10.11.35.0")])]});
            hole(context, id + "F3", {"style" : HoleStyle.SIMPLE, "endStyle" : HoleEndStyle.THROUGH, "holeDiameter" : 4 * mm, "majorDiameter" : 6.35 * mm, "isTappedThrough" : true, "tappedDepth" : 12.7 * mm, "tapClearance" : 3, "locations" : qUnion([Q0]), "scope" : qUnion([Q1])});
        }
    });
